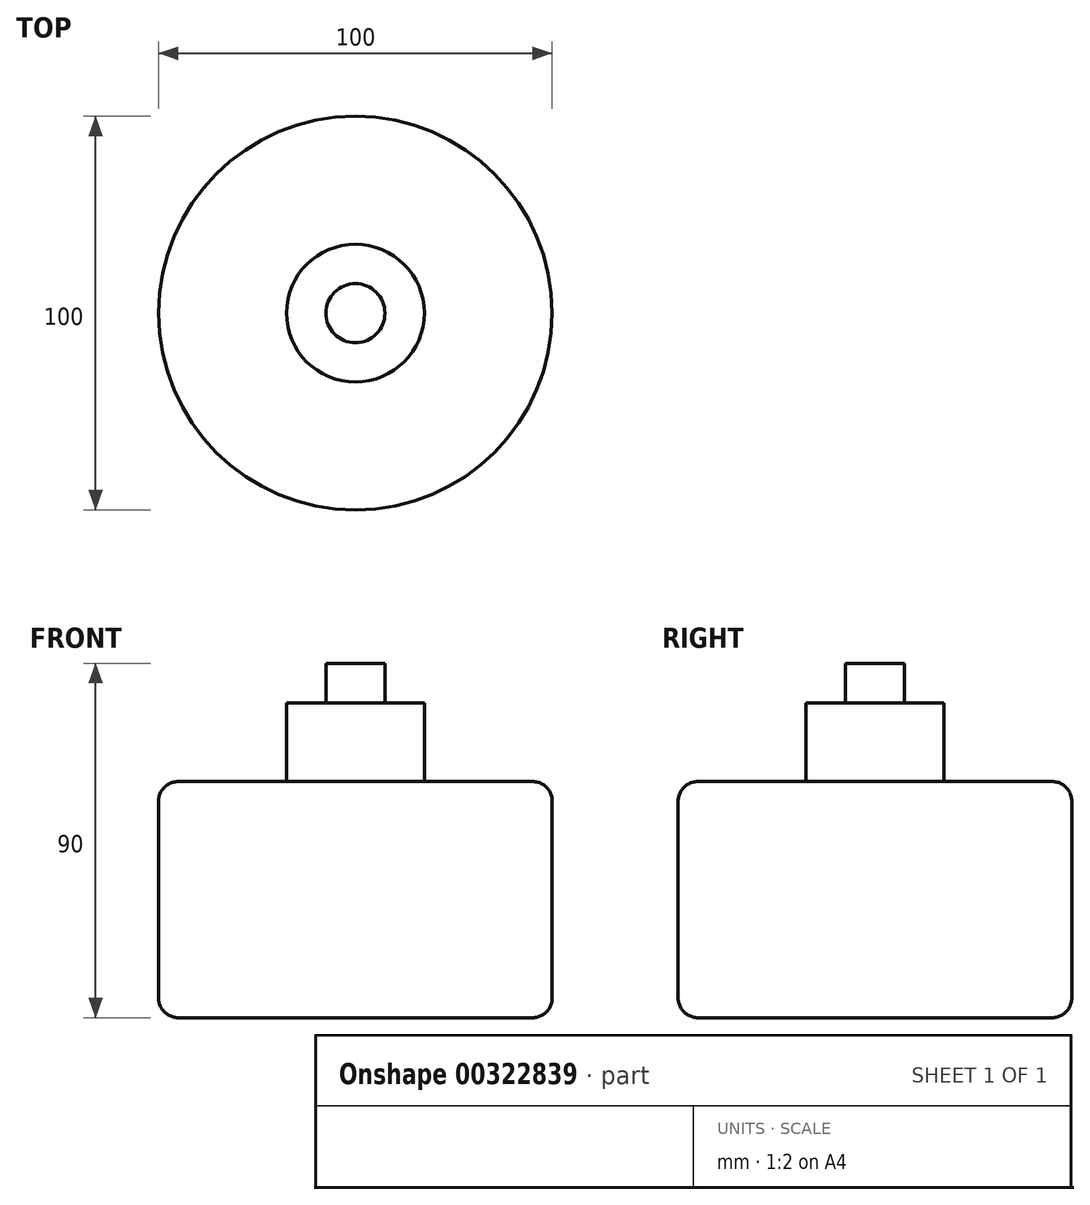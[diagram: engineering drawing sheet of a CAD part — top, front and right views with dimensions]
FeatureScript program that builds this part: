
annotation { "Feature Type Name" : "Feature", "Feature Type Description" : "" }
export const myFeature = defineFeature(function(context is Context, id is Id, definition is map)
    precondition{}
    {
        {
            var Q0;
            Q0=qCreatedBy(makeId("Top.planeOp"),FACE);
            var sketch = newSketch(context, id + "F0", { "sketchPlane" : qUnion([Q0])});
            skCircle(sketch, "E0", {"center": v(0, 0) * mm, "radius": 50 * mm});
            skSolve(sketch);
        }
        {
            var Q0;
            Q0=makeQuery(id+"F0.imprint","IMPRINT",FACE,{"disambiguationData":[TD([[makeQuery(id+"F0.imprint","IMPRINT",EDGE,{"derivedFrom":sQuery(id+"F0.wireOp",EDGE,"E0")}),1.0]])]});
            extrude(context, id + "F1", {"entities" : qUnion([Q0]), "depth" : 60 * mm});
        }
        {
            var Q0;
            Q0=makeQuery(id+"F1.opExtrude","CAP_EDGE",EDGE,{"disambiguationData":[OSD([sQuery(id+"F0.wireOp",EDGE,"E0")])],"isStart":false});
            var Q1;
            Q1=makeQuery(id+"F1.opExtrude","CAP_EDGE",EDGE,{"disambiguationData":[OSD([sQuery(id+"F0.wireOp",EDGE,"E0")])],"isStart":true});
            fillet(context, id + "F2", {"entities" : qUnion([Q0, Q1]), "radius" : 5 * mm, "tangentPropagation" : true, "allowEdgeOverflow" : false});
        }
        {
            var Q0;
            Q0=makeQuery(id+"F1.opExtrude","CAP_FACE",FACE,{"disambiguationData":[OSD([sQuery(id+"F0.wireOp",EDGE,"E0")])],"isStart":false});
            var sketch = newSketch(context, id + "F3", { "sketchPlane" : qUnion([Q0])});
            skCircle(sketch, "E1", {"center": v(0, 0) * mm, "radius": 17.5 * mm});
            skSolve(sketch);
        }
        {
            var Q0;
            Q0=makeQuery(id+"F3.imprint","IMPRINT",FACE,{"disambiguationData":[TD([[makeQuery(id+"F3.imprint","IMPRINT",EDGE,{"derivedFrom":sQuery(id+"F3.wireOp",EDGE,"E1")}),1.0]])]});
            extrude(context, id + "F4", {"entities" : qUnion([Q0]), "operationType" : NewBodyOperationType.ADD, "depth" : 20 * mm});
        }
        {
            var Q0;
            Q0=makeQuery(id+"F4.opExtrude","CAP_FACE",FACE,{"disambiguationData":[OSD([sQuery(id+"F3.wireOp",EDGE,"E1")])],"isStart":false});
            var sketch = newSketch(context, id + "F5", { "sketchPlane" : qUnion([Q0])});
            skCircle(sketch, "E2", {"center": v(0, 0) * mm, "radius": 7.5 * mm});
            skSolve(sketch);
        }
        {
            var Q0;
            Q0=makeQuery(id+"F5.imprint","IMPRINT",FACE,{"disambiguationData":[TD([[makeQuery(id+"F5.imprint","IMPRINT",EDGE,{"derivedFrom":sQuery(id+"F5.wireOp",EDGE,"E2")}),1.0]])]});
            extrude(context, id + "F6", {"entities" : qUnion([Q0]), "operationType" : NewBodyOperationType.ADD, "depth" : 10 * mm});
        }
    });
